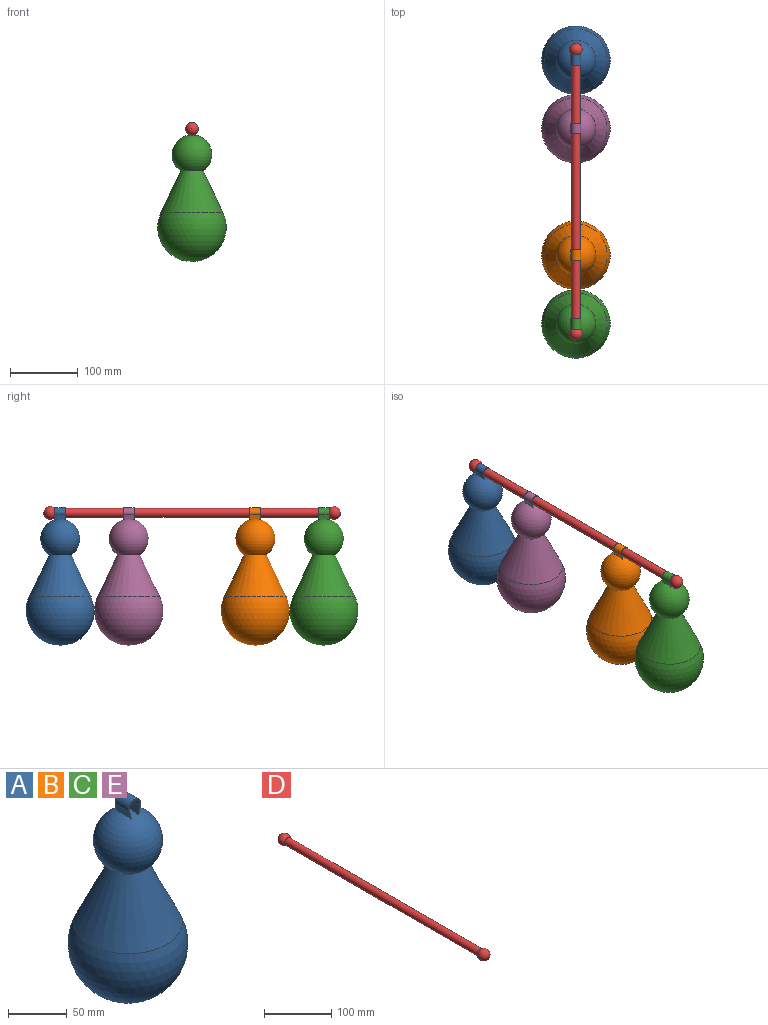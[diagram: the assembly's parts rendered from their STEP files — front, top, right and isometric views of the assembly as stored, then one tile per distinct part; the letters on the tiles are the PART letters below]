
ASSEMBLY  parts=5 mates=1
PART A: 11 faces, bbox 101.6x101.6x204.1 mm
  f0: sphere r=29.44mm, area 9875.8mm2, adj f1,f4,f5,f7,f8,f9,f10
  f1: cone r=16.86mm half-angle=25.2deg, axis (0,0,-1), area 13478.5mm2, adj f0,f2
  f2: sphere r=50.8mm, area 23122.6mm2, adj f1
  f3: cylinder r=7.37mm len=15.88mm, axis (0,1,0), area 426.5mm2, adj f4,f8,f9,f10
  f4: plane 15.88x8.64mm, normal (-0.97,0,-0.25), area 130.1mm2, adj f0,f3,f9,f10
  f5: plane 15.88x8.74mm, normal (0.97,0,0.25), area 131.6mm2, adj f0,f6,f9,f10
  f6: cylinder r=6.35mm len=15.88mm, axis (0,1,0), area 367.6mm2, adj f5,f7,f9,f10
  f7: plane 15.88x8.74mm, normal (-0.97,0,0.25), area 131.6mm2, adj f0,f6,f9,f10
  f8: plane 15.88x8.64mm, normal (0.97,0,-0.25), area 130.1mm2, adj f0,f3,f9,f10
  f9: plane 17.85x14.73mm, normal (0,-1,0), area 43.6mm2, adj f0,f3,f4,f5,f6,f7,f8
  f10: plane 17.85x14.73mm, normal (0,1,0), area 43.6mm2, adj f0,f3,f4,f5,f6,f7,f8
PART B: same geometry as A
PART C: same geometry as A
PART D: 3 faces, bbox 19.1x439.6x19.1 mm
  f0: sphere r=9.53mm, area 994.9mm2, adj f1
  f1: cylinder r=6.35mm len=406.4mm, axis (0,-1,0), area 16214.6mm2, adj f0,f2
  f2: sphere r=9.53mm, area 994.9mm2, adj f1
PART E: same geometry as A
PLACE A t=(0,390.65,0)mm
PLACE B t=(0,101.6,0)mm
PLACE C at identity
PLACE D at identity fixed
PLACE E t=(0,289.05,0)mm
MATE fastened C.f3 <-> D.f1  axis (0,-1,0) through (0,-203.2,419.1)mm
